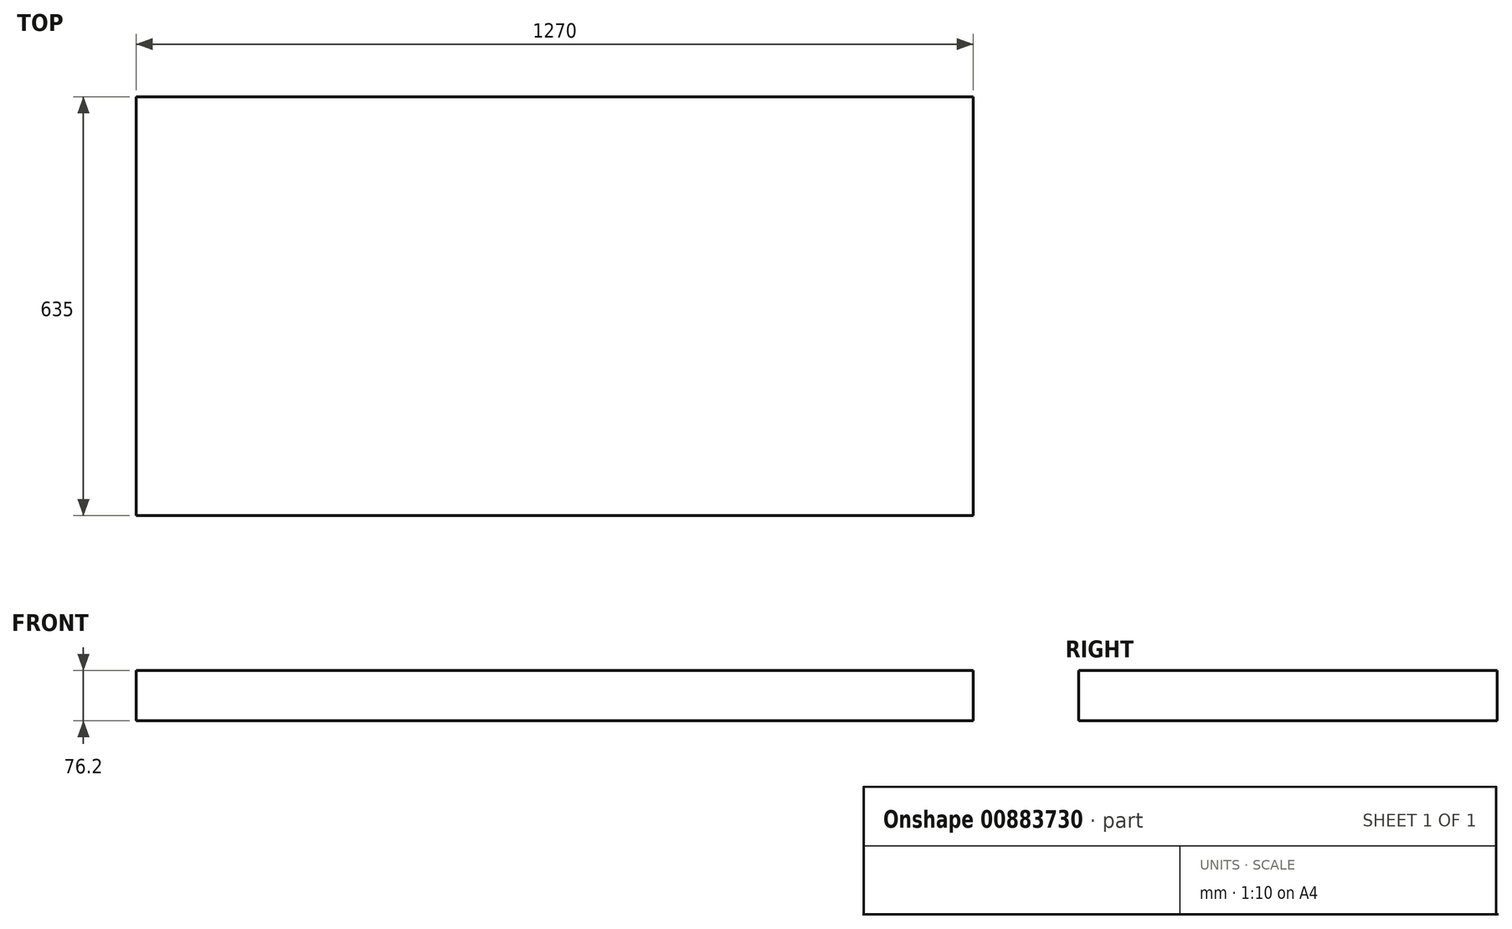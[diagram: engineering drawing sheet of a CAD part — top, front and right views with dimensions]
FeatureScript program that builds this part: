
annotation { "Feature Type Name" : "Feature", "Feature Type Description" : "" }
export const myFeature = defineFeature(function(context is Context, id is Id, definition is map)
    precondition{}
    {
        {
            var Q0;
            Q0=qCreatedBy(makeId("Top.planeOp"),FACE);
            var sketch = newSketch(context, id + "F0", { "sketchPlane" : qUnion([Q0])});
            skLineSegment(sketch, "E0.bottom", {"start": v(0, 0) * mm, "end": v(1270, 0) * mm});
            skLineSegment(sketch, "E0.top", {"start": v(0, 635) * mm, "end": v(1270, 635) * mm});
            skLineSegment(sketch, "E0.left", {"start": v(0, 0) * mm, "end": v(0, 635) * mm});
            skLineSegment(sketch, "E0.right", {"start": v(1270, 0) * mm, "end": v(1270, 635) * mm});
            skSolve(sketch);
        }
        {
            var Q0;
            Q0 = qSketchRegion(id + "F0", true);
            extrude(context, id + "F1", {"entities" : qUnion([Q0]), "depth" : 76.2 * mm, "offsetDistance" : 25.4 * mm});
        }
    });
